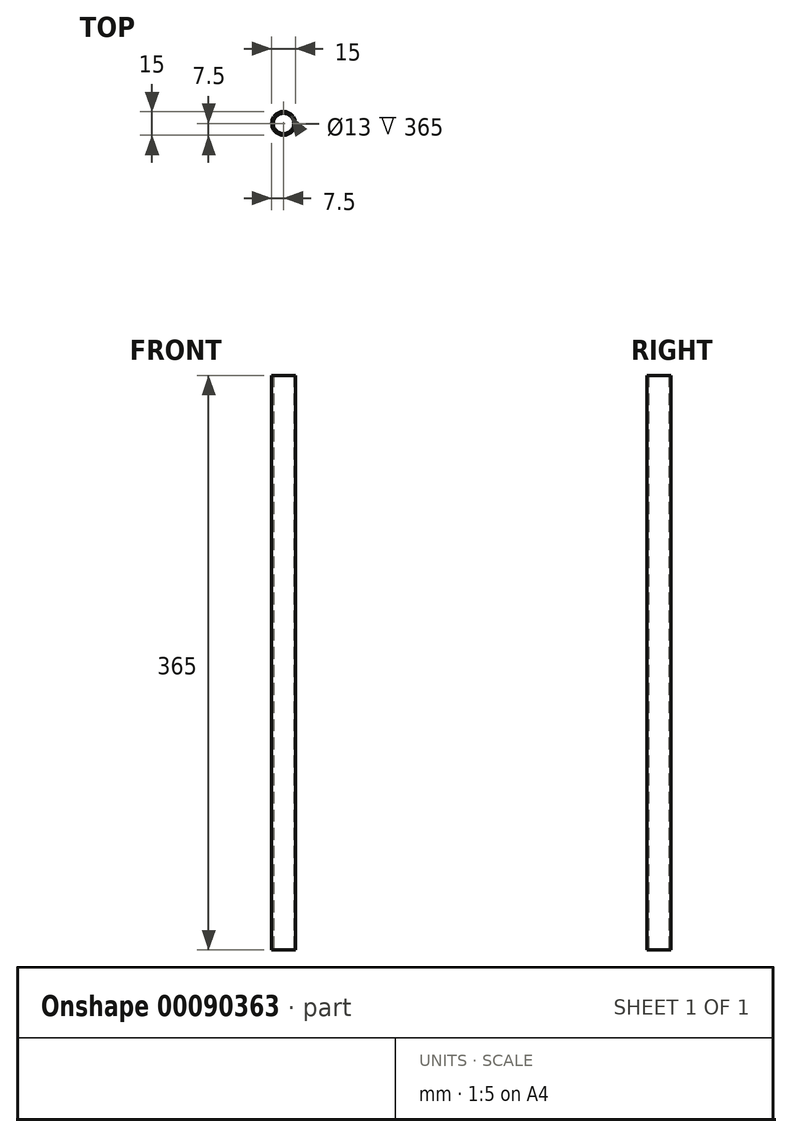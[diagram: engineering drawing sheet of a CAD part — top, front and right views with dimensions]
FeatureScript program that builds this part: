
annotation { "Feature Type Name" : "Feature", "Feature Type Description" : "" }
export const myFeature = defineFeature(function(context is Context, id is Id, definition is map)
    precondition{}
    {
        {
            var Q0;
            Q0=qCreatedBy(makeId("Top.planeOp"),FACE);
            var sketch = newSketch(context, id + "F0", { "sketchPlane" : qUnion([Q0])});
            skCircle(sketch, "E0", {"center": v(0, 0) * mm, "radius": 7.5 * mm});
            skCircle(sketch, "E1.0", {"center": v(0, 0) * mm, "radius": 6.5 * mm});
            skSolve(sketch);
        }
        {
            var Q0;
            Q0=qCreatedBy(makeId("Front.planeOp"),FACE);
            var sketch = newSketch(context, id + "F1", { "sketchPlane" : qUnion([Q0])});
            skSolve(sketch);
        }
        {
            var Q0;
            Q0 = qSketchRegion(id + "F1", true);
            var Q1;
            Q1=makeQuery(id+"F0.imprint","IMPRINT",FACE,{"disambiguationData":[TD([[makeQuery(id+"F0.imprint","IMPRINT",EDGE,{"derivedFrom":sQuery(id+"F0.wireOp",EDGE,"E0")}),1.0]])]});
            extrude(context, id + "F2", {"entities" : qUnion([Q0, Q1]), "depth" : (380 - 15) * mm});
        }
    });
